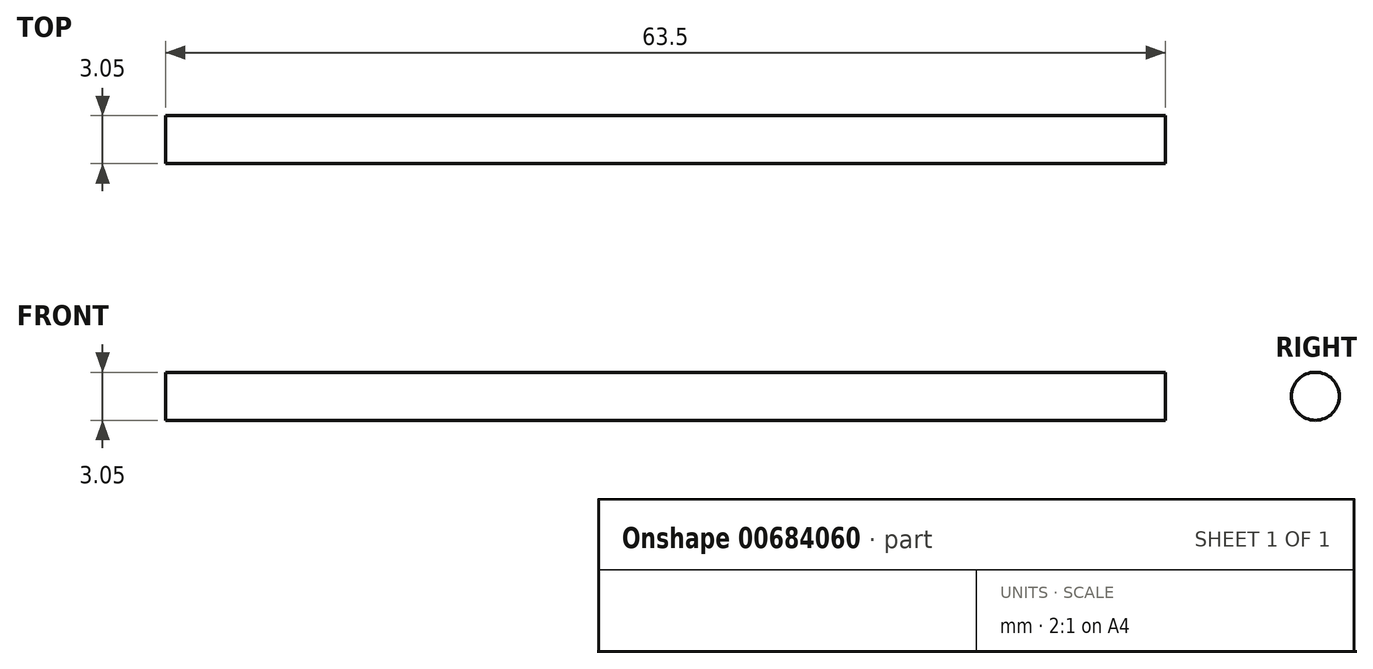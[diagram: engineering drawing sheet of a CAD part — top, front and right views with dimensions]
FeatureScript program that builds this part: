
annotation { "Feature Type Name" : "Feature", "Feature Type Description" : "" }
export const myFeature = defineFeature(function(context is Context, id is Id, definition is map)
    precondition{}
    {
        {
            var Q0;
            Q0=qCreatedBy(makeId("Right.planeOp"),FACE);
            var sketch = newSketch(context, id + "F0", { "sketchPlane" : qUnion([Q0])});
            skCircle(sketch, "E0", {"center": v(-27.05, 31.88) * mm, "radius": 1.52 * mm});
            skSolve(sketch);
        }
        {
            var Q0;
            Q0=makeQuery(id+"F0.imprint","IMPRINT",FACE,{"disambiguationData":[TD([[makeQuery(id+"F0.imprint","IMPRINT",EDGE,{"derivedFrom":sQuery(id+"F0.wireOp",EDGE,"E0")}),1.0]])]});
            extrude(context, id + "F1", {"entities" : qUnion([Q0]), "depth" : 63.5 * mm, "offsetDistance" : 25.4 * mm});
        }
    });
